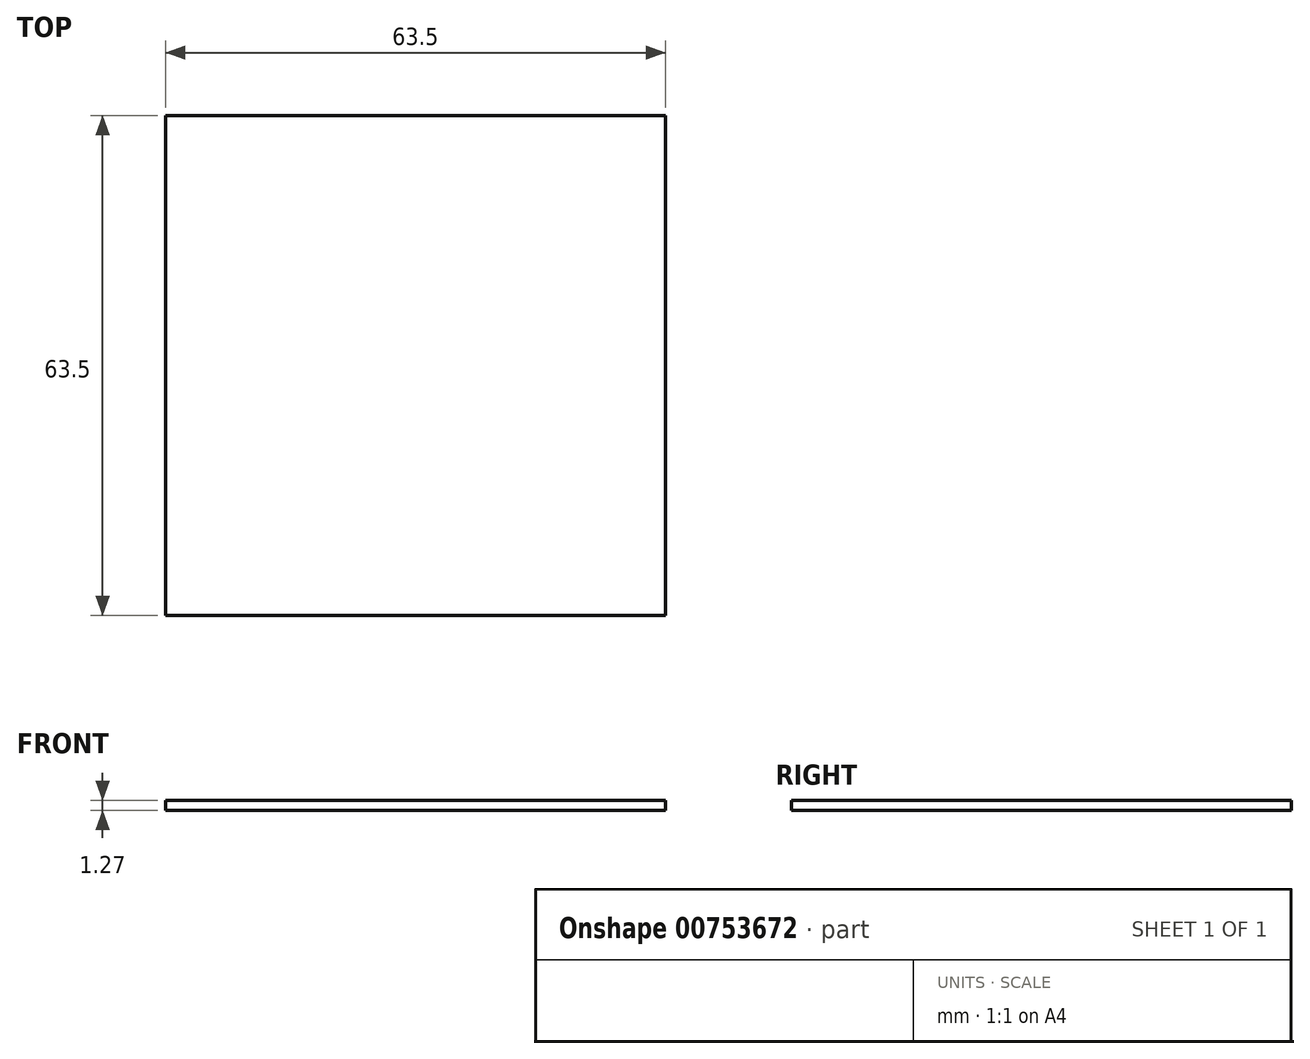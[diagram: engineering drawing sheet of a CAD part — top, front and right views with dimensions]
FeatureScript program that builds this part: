
annotation { "Feature Type Name" : "Feature", "Feature Type Description" : "" }
export const myFeature = defineFeature(function(context is Context, id is Id, definition is map)
    precondition{}
    {
        {
            var Q0;
            Q0=qCreatedBy(makeId("Top.planeOp"),FACE);
            var sketch = newSketch(context, id + "F0", { "sketchPlane" : qUnion([Q0])});
            skLineSegment(sketch, "E0.bottom", {"start": v(-31.45, 48.25) * mm, "end": v(32.05, 48.25) * mm});
            skLineSegment(sketch, "E0.top", {"start": v(-31.45, -15.25) * mm, "end": v(32.05, -15.25) * mm});
            skLineSegment(sketch, "E0.left", {"start": v(-31.45, 48.25) * mm, "end": v(-31.45, -15.25) * mm});
            skLineSegment(sketch, "E0.right", {"start": v(32.05, 48.25) * mm, "end": v(32.05, -15.25) * mm});
            skSolve(sketch);
        }
        {
            var Q0;
            Q0 = qSketchRegion(id + "F0", true);
            extrude(context, id + "F1", {"entities" : qUnion([Q0]), "depth" : 1.27 * mm, "offsetDistance" : 25.4 * mm});
        }
    });
